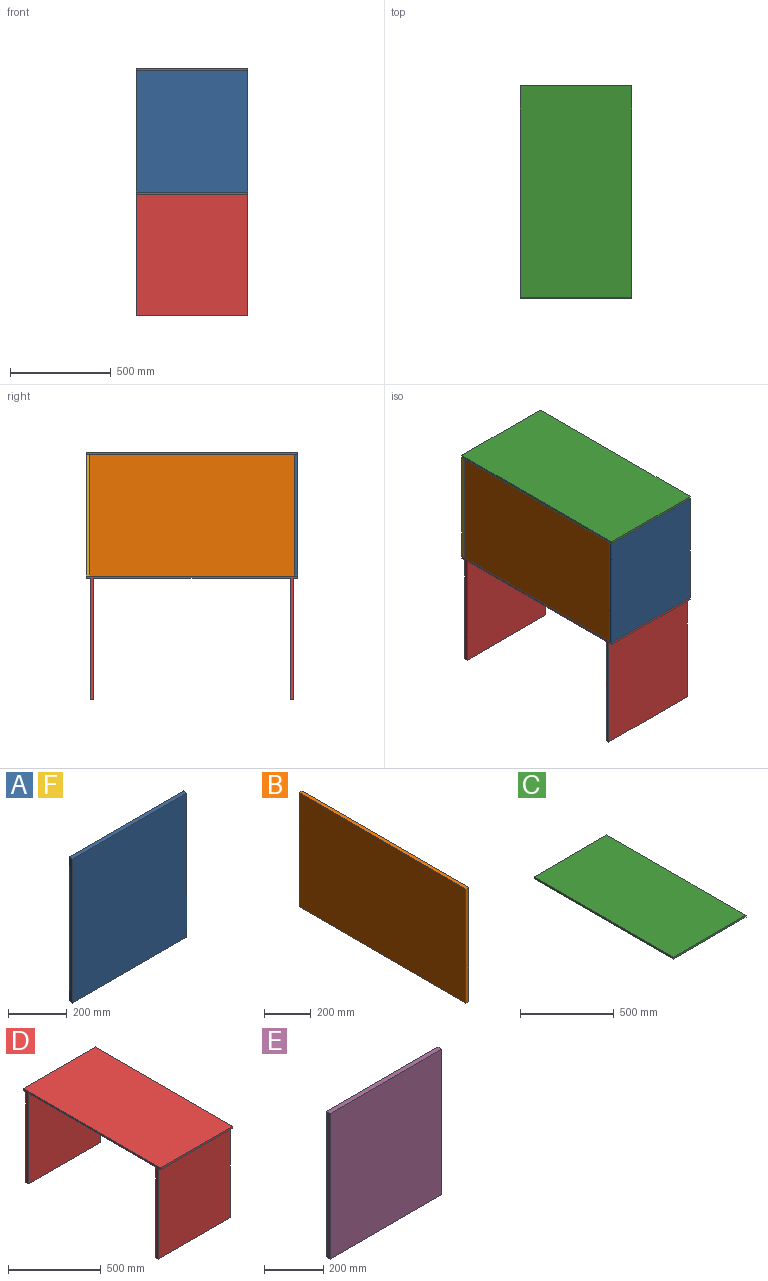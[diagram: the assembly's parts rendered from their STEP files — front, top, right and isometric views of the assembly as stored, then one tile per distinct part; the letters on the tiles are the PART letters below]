
ASSEMBLY  parts=6 mates=5
PART A: 6 faces, bbox 550x18x600 mm
  f0: plane 600x18mm, normal (1,0,0), area 10800mm2, adj f1,f3,f4,f5
  f1: plane 600x550mm, normal (0,-1,0), area 330000mm2, adj f0,f2,f4,f5
  f2: plane 600x18mm, normal (-1,0,0), area 10800mm2, adj f1,f3,f4,f5
  f3: plane 600x550mm, normal (0,1,0), area 330000mm2, adj f0,f2,f4,f5
  f4: plane 550x18mm, normal (0,0,-1), area 9900mm2, adj f0,f1,f2,f3
  f5: plane 550x18mm, normal (0,0,1), area 9900mm2, adj f0,f1,f2,f3
PART B: 6 faces, bbox 18x1014x600 mm
  f0: plane 600x18mm, normal (0,1,0), area 10800mm2, adj f1,f3,f4,f5
  f1: plane 1014x18mm, normal (0,0,-1), area 18252mm2, adj f0,f2,f4,f5
  f2: plane 600x18mm, normal (0,-1,0), area 10800mm2, adj f1,f3,f4,f5
  f3: plane 1014x18mm, normal (0,0,1), area 18252mm2, adj f0,f2,f4,f5
  f4: plane 1014x600mm, normal (1,0,0), area 608400.2mm2, adj f0,f1,f2,f3
  f5: plane 1014x600mm, normal (-1,0,0), area 608400.2mm2, adj f0,f1,f2,f3
PART C: 6 faces, bbox 550x1050x12 mm
  f0: plane 550x12mm, normal (0,-1,0), area 6600mm2, adj f1,f3,f4,f5
  f1: plane 1050x12mm, normal (1,0,0), area 12600mm2, adj f0,f2,f4,f5
  f2: plane 550x12mm, normal (0,1,0), area 6600mm2, adj f1,f3,f4,f5
  f3: plane 1050x12mm, normal (-1,0,0), area 12600mm2, adj f0,f2,f4,f5
  f4: plane 1050x550mm, normal (0,0,1), area 577500mm2, adj f0,f1,f2,f3
  f5: plane 1050x550mm, normal (0,0,-1), area 577500mm2, adj f0,f1,f2,f3
PART D: 14 faces, bbox 550x1050x612 mm
  f0: plane 974x550mm, normal (0,0,-1), area 535700mm2, adj f3,f5,f9,f12
  f1: plane 550x20mm, normal (0,0,-1), area 11000mm2, adj f2,f3,f5,f8
  f2: plane 550x12mm, normal (0,-1,0), area 6600mm2, adj f1,f3,f5,f6
  f3: plane 1050x612mm, normal (1,0,0), area 34200mm2, adj f0,f1,f2,f4,f6,f7,f8,f9
  f4: plane 550x12mm, normal (0,1,0), area 6600mm2, adj f3,f5,f6,f7
  f5: plane 1050x612mm, normal (-1,0,0), area 34200mm2, adj f0,f1,f2,f4,f6,f7,f8,f9
  f6: plane 1050x550mm, normal (0,0,1), area 577500mm2, adj f2,f3,f4,f5
  f7: plane 550x20mm, normal (0,0,-1), area 11000mm2, adj f3,f4,f5,f11
  f8: plane 600x550mm, normal (0,-1,0), area 330000mm2, adj f1,f3,f5,f10
  f9: plane 600x550mm, normal (0,1,0), area 330000mm2, adj f0,f3,f5,f10
  f10: plane 550x18mm, normal (0,0,-1), area 9900mm2, adj f3,f5,f8,f9
  f11: plane 600x550mm, normal (0,1,0), area 330000mm2, adj f3,f5,f7,f13
  f12: plane 600x550mm, normal (0,-1,0), area 330000mm2, adj f0,f3,f5,f13
  f13: plane 550x18mm, normal (0,0,-1), area 9900mm2, adj f3,f5,f11,f12
PART E: 6 faces, bbox 532x18x600 mm
  f0: plane 600x18mm, normal (1,0,0), area 10800mm2, adj f1,f3,f4,f5
  f1: plane 600x532mm, normal (0,-1,0), area 319200mm2, adj f0,f2,f4,f5
  f2: plane 600x18mm, normal (-1,0,0), area 10800mm2, adj f1,f3,f4,f5
  f3: plane 600x532mm, normal (0,1,0), area 319200mm2, adj f0,f2,f4,f5
  f4: plane 532x18mm, normal (0,0,-1), area 9576mm2, adj f0,f1,f2,f3
  f5: plane 532x18mm, normal (0,0,1), area 9576mm2, adj f0,f1,f2,f3
PART F: same geometry as A
PLACE A t=(186.24,-1040.4,-973.92)mm
PLACE B t=(186.24,-8.4,-973.92)mm
PLACE C t=(186.24,-8.4,-973.92)mm
PLACE D t=(186.24,-8.4,-1585.92)mm
PLACE E t=(185,-34.09,-973.92)mm
PLACE F t=(186.24,-8.4,-973.92)mm
MATE fastened B.f0 <-> F.f1  axis (0,1,0) through (-88.76,498.6,-973.92)mm
MATE fastened F.f5 <-> C.f5  axis (0,0,1) through (461.24,516.6,-973.92)mm
MATE fastened F.f4 <-> D.f6  axis (0,0,-1) through (461.24,516.6,-1573.92)mm
MATE fastened A.f4 <-> D.f6  axis (0,0,-1) through (461.24,-533.4,-1573.92)mm
MATE planar E.f4 <-> D.f6  axis (0,0,-1) through (194,81.91,-1573.92)mm
